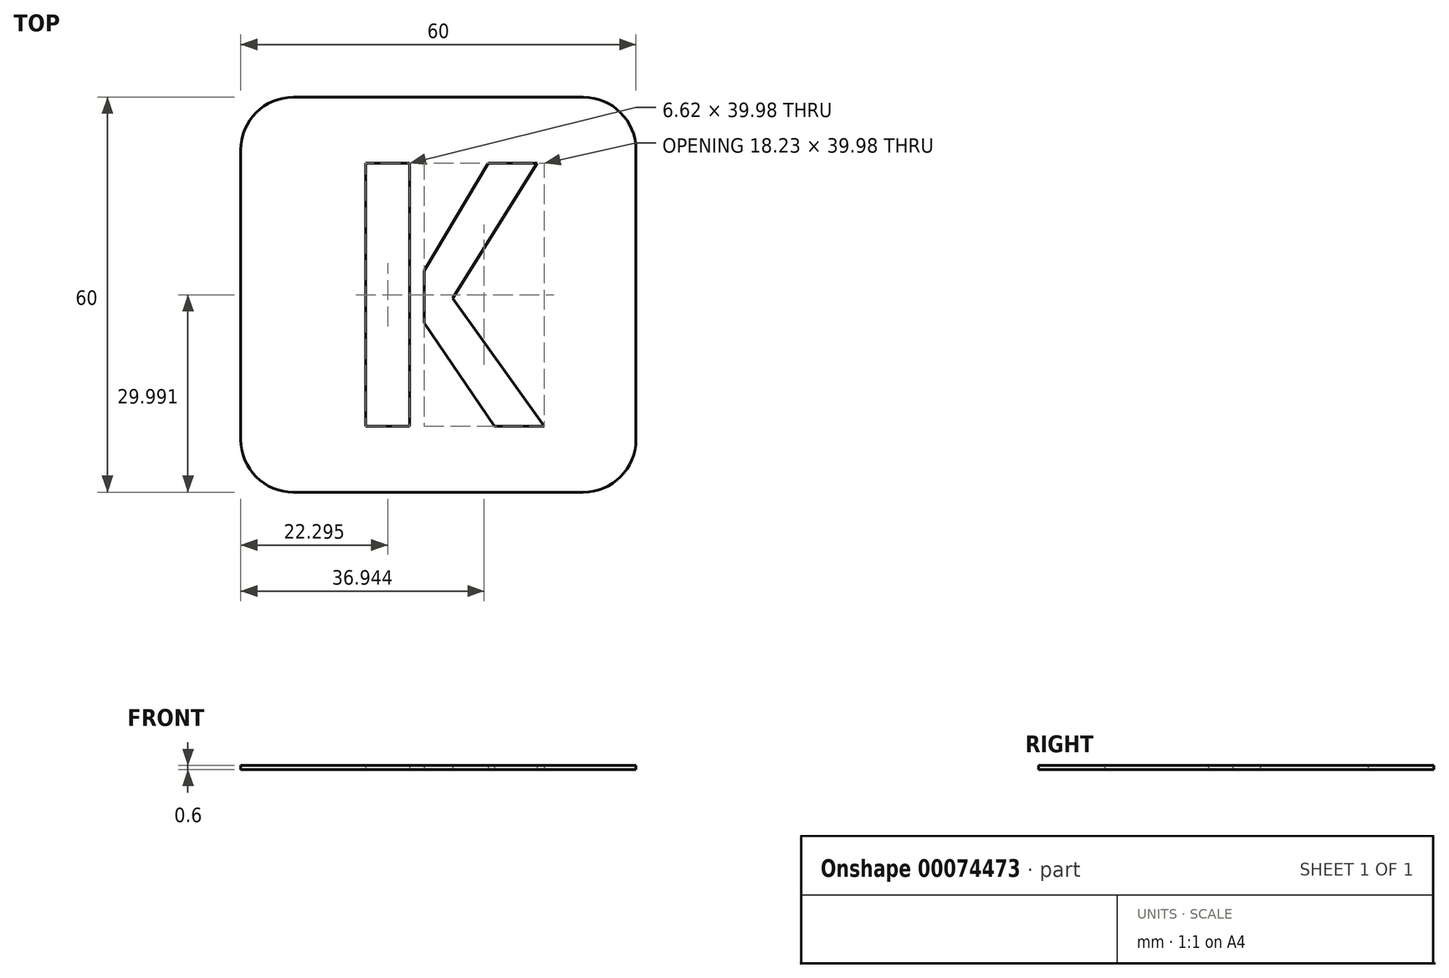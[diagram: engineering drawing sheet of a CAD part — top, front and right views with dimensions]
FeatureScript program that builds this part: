
annotation { "Feature Type Name" : "Feature", "Feature Type Description" : "" }
export const myFeature = defineFeature(function(context is Context, id is Id, definition is map)
    precondition{}
    {
        {
            var Q0;
            Q0=qCreatedBy(makeId("Top.planeOp"),FACE);
            var sketch = newSketch(context, id + "F0", { "sketchPlane" : qUnion([Q0])});
            skLineSegment(sketch, "E0.rect.bottom", {"start": v(16.06, -20) * mm, "end": v(-16.06, -20) * mm});
            skLineSegment(sketch, "E0.rect.top", {"start": v(16.06, 20) * mm, "end": v(-16.06, 20) * mm});
            skLineSegment(sketch, "E0.rect.left", {"start": v(16.06, -20) * mm, "end": v(16.06, 20) * mm});
            skLineSegment(sketch, "E0.rect.right", {"start": v(-16.06, -20) * mm, "end": v(-16.06, 20) * mm});
            skPoint(sketch, "E0.rect.middle", {"position": v(0, 0) * mm});
            skText(sketch, "E1", { "text": "K", "fontName": "AllertaStencil-Regular.ttf"});
            skLineSegment(sketch, "E2.rect.bottom", {"start": v(30, -30) * mm, "end": v(-30, -30) * mm});
            skLineSegment(sketch, "E2.rect.top", {"start": v(30, 30) * mm, "end": v(-30, 30) * mm});
            skLineSegment(sketch, "E2.rect.left", {"start": v(30, -30) * mm, "end": v(30, 30) * mm});
            skLineSegment(sketch, "E2.rect.right", {"start": v(-30, -30) * mm, "end": v(-30, 30) * mm});
            const initialGuessF0  = {"E1": [-0.01606, -0.02, 1, 0, 0.04]};
            skSetInitialGuess(sketch, initialGuessF0);
            skSolve(sketch);
        }
        {
            var Q0;
            Q0=makeQuery(id+"F0.imprint","IMPRINT",FACE,{"disambiguationData":[TD([[makeQuery(id+"F0.imprint","IMPRINT",EDGE,{"derivedFrom":sQuery(id+"F0.wireOp",EDGE,"E0.rect.top")}),1.0]])]});
            var Q1;
            Q1=makeQuery(id+"F0.imprint","IMPRINT",FACE,{"disambiguationData":[TD([[makeQuery(id+"F0.imprint","IMPRINT",EDGE,{"derivedFrom":sQuery(id+"F0.wireOp",EDGE,"E0.rect.top")}),-1.0]])]});
            extrude(context, id + "F1", {"entities" : qUnion([Q0, Q1]), "depth" : 0.6 * mm});
        }
        {
            var Q0;
            Q0=makeQuery(id+"F1.opExtrude","SWEPT_EDGE",EDGE,{"disambiguationData":[OSD([sQuery(id+"F0.wireOp",EDGE,"E2.rect.top"),sQuery(id+"F0.wireOp",EDGE,"E2.rect.right")])]});
            var Q1;
            Q1=makeQuery(id+"F1.opExtrude","SWEPT_EDGE",EDGE,{"disambiguationData":[OSD([sQuery(id+"F0.wireOp",EDGE,"E2.rect.top"),sQuery(id+"F0.wireOp",EDGE,"E2.rect.left")])]});
            var Q2;
            Q2=makeQuery(id+"F1.opExtrude","SWEPT_EDGE",EDGE,{"disambiguationData":[OSD([sQuery(id+"F0.wireOp",EDGE,"E2.rect.bottom"),sQuery(id+"F0.wireOp",EDGE,"E2.rect.left")])]});
            var Q3;
            Q3=makeQuery(id+"F1.opExtrude","SWEPT_EDGE",EDGE,{"disambiguationData":[OSD([sQuery(id+"F0.wireOp",EDGE,"E2.rect.bottom"),sQuery(id+"F0.wireOp",EDGE,"E2.rect.right")])]});
            fillet(context, id + "F2", {"entities" : qUnion([Q0, Q1, Q2, Q3]), "radius" : 8 * mm, "tangentPropagation" : true, "allowEdgeOverflow" : false});
        }
    });
